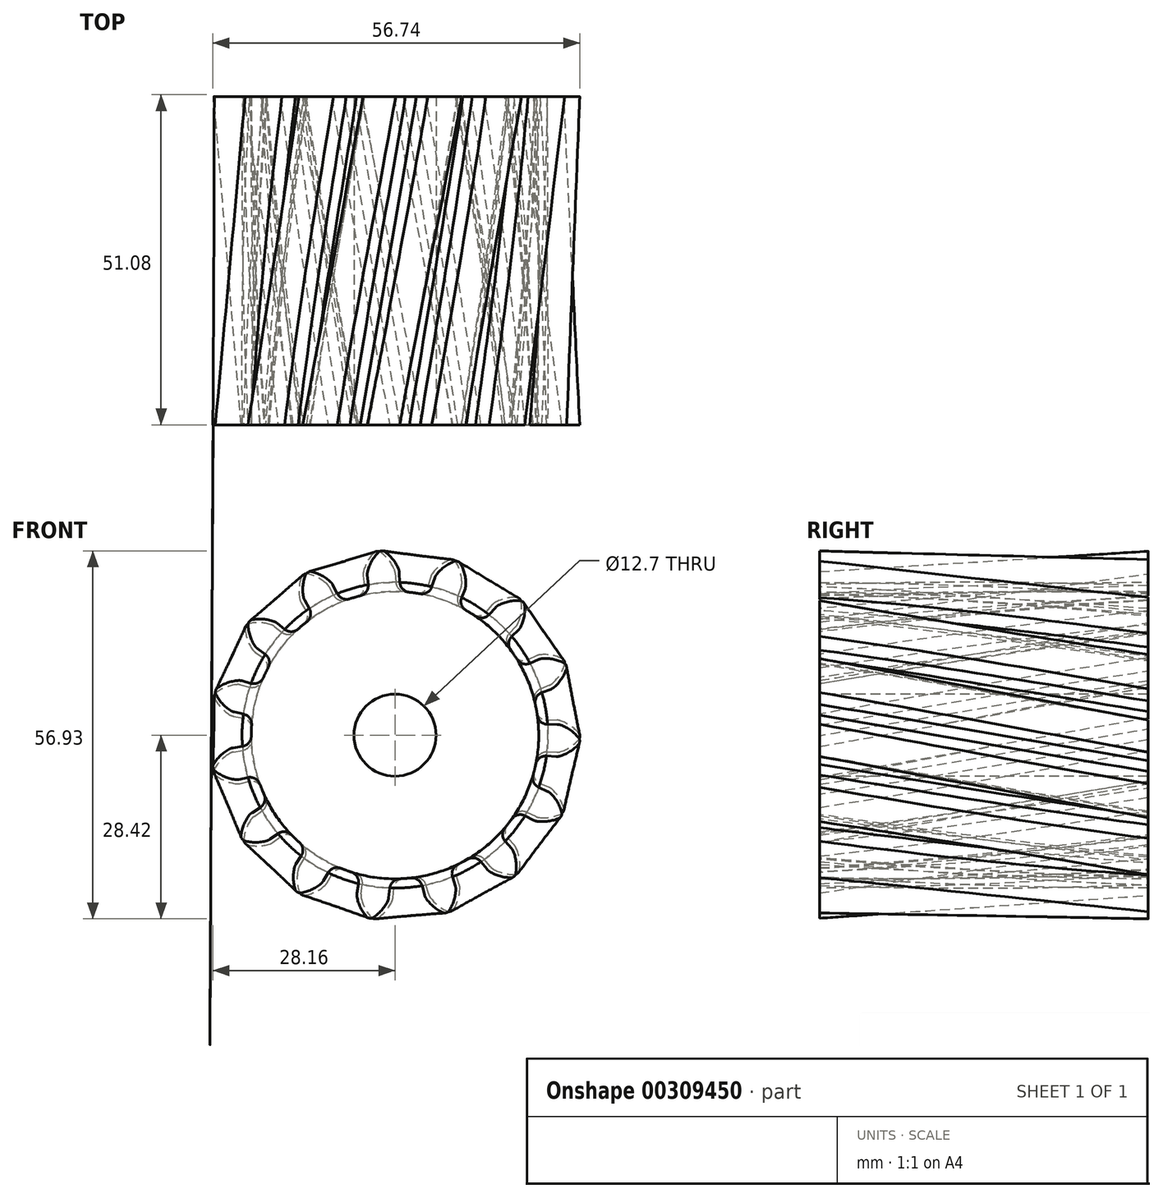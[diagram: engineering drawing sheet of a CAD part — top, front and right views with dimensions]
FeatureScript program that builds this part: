
annotation { "Feature Type Name" : "Feature", "Feature Type Description" : "" }
export const myFeature = defineFeature(function(context is Context, id is Id, definition is map)
    precondition{}
    {
        {
            var Q0;
            Q0=qCreatedBy(makeId("Front.planeOp"),FACE);
            var sketch = newSketch(context, id + "F0", { "sketchPlane" : qUnion([Q0])});
            skCircle(sketch, "E0", {"center": v(0, 0) * mm, "radius": 22.23 * mm});
            skArc(sketch, "E1.trimOffspring", {"start": v(-0.11, 25.67) * mm, "mid": v(-1.04, 27.17) * mm, "end": v(-2.34, 28.36) * mm});
            skLineSegment(sketch, "E2", {"start": v(0.02, 25.15) * mm, "end": v(0.23, 22.22) * mm});
            skLineSegment(sketch, "E3", {"start": v(-2.68, 28.45) * mm, "end": v(-2.8, 28.44) * mm});
            skLineSegment(sketch, "E4.MirrorCS", {"start": v(-2.93, 28.43) * mm, "end": v(-2.8, 28.44) * mm});
            skArc(sketch, "E5.MirrorCS", {"start": v(-4.9, 25.2) * mm, "mid": v(-4.28, 26.86) * mm, "end": v(-3.23, 28.28) * mm});
            skLineSegment(sketch, "E6.MirrorCS", {"start": v(-4.92, 24.66) * mm, "end": v(-4.56, 21.75) * mm});
            skPoint(sketch, "E7.visualSharp", {"position": v(0, 25.4) * mm});
            skArc(sketch, "E7.filletArc", {"start": v(0.02, 25.15) * mm, "mid": v(-0.02, 25.41) * mm, "end": v(-0.11, 25.67) * mm});
            skPoint(sketch, "E8.visualSharp", {"position": v(-4.96, 24.91) * mm});
            skArc(sketch, "E8.filletArc", {"start": v(-4.9, 25.2) * mm, "mid": v(-4.93, 24.93) * mm, "end": v(-4.92, 24.66) * mm});
            skPoint(sketch, "E9.visualSharp", {"position": v(-2.5, 28.47) * mm});
            skArc(sketch, "E9.filletArc", {"start": v(-2.34, 28.36) * mm, "mid": v(-2.5, 28.44) * mm, "end": v(-2.68, 28.45) * mm});
            skPoint(sketch, "E10.visualSharp", {"position": v(-3.1, 28.4) * mm});
            skArc(sketch, "E10.filletArc", {"start": v(-2.93, 28.43) * mm, "mid": v(-3.1, 28.38) * mm, "end": v(-3.23, 28.28) * mm});
            skSolve(sketch);
        }
        {
            var Q0;
            Q0=qCreatedBy(makeId("Front.planeOp"),FACE);
            cPlane(context, id + "F1", {"entities" : qUnion([Q0]), "cplaneType" : CPlaneType.OFFSET, "offset" : 50.8 * mm, "width" : 152.4 * mm, "height" : 152.4 * mm});
        }
        {
            var Q0;
            Q0=qCreatedBy(id+"F1.planeOp",FACE);
            var sketch = newSketch(context, id + "F2", { "sketchPlane" : qUnion([Q0])});
            skArc(sketch, "E11.0.0", {"start": v(-4.56, 21.75) * mm, "mid": v(2.18, -22.12) * mm, "end": v(0.23, 22.22) * mm});
            skArc(sketch, "E11.0.1", {"start": v(0.23, 22.22) * mm, "mid": v(-2.18, 22.12) * mm, "end": v(-4.56, 21.75) * mm});
            skArc(sketch, "E12.0.0", {"start": v(-3.23, 28.28) * mm, "mid": v(-4.28, 26.86) * mm, "end": v(-4.9, 25.2) * mm});
            skArc(sketch, "E12.0.1", {"start": v(-4.9, 25.2) * mm, "mid": v(-4.93, 24.93) * mm, "end": v(-4.92, 24.66) * mm});
            skLineSegment(sketch, "E12.0.2", {"start": v(-4.92, 24.66) * mm, "end": v(-4.56, 21.75) * mm});
            skArc(sketch, "E12.0.3", {"start": v(-4.56, 21.75) * mm, "mid": v(-2.18, 22.12) * mm, "end": v(0.23, 22.22) * mm});
            skLineSegment(sketch, "E12.0.4", {"start": v(0.23, 22.22) * mm, "end": v(0.02, 25.15) * mm});
            skArc(sketch, "E12.0.5", {"start": v(0.02, 25.15) * mm, "mid": v(-0.02, 25.41) * mm, "end": v(-0.11, 25.67) * mm});
            skArc(sketch, "E12.0.6", {"start": v(-0.11, 25.67) * mm, "mid": v(-1.04, 27.17) * mm, "end": v(-2.34, 28.36) * mm});
            skArc(sketch, "E12.0.7", {"start": v(-2.34, 28.36) * mm, "mid": v(-2.5, 28.44) * mm, "end": v(-2.68, 28.45) * mm});
            skLineSegment(sketch, "E12.0.8", {"start": v(-2.68, 28.45) * mm, "end": v(-2.8, 28.44) * mm});
            skLineSegment(sketch, "E12.0.9", {"start": v(-2.8, 28.44) * mm, "end": v(-2.93, 28.43) * mm});
            skArc(sketch, "E12.0.10", {"start": v(-2.93, 28.43) * mm, "mid": v(-3.1, 28.38) * mm, "end": v(-3.23, 28.28) * mm});
            skLineSegment(sketch, "E13.1.0", {"start": v(-8.3, 20.62) * mm, "end": v(-9.6, 23.24) * mm});
            skArc(sketch, "E13.1.1", {"start": v(-9.6, 23.24) * mm, "mid": v(-9.75, 23.47) * mm, "end": v(-9.93, 23.68) * mm});
            skArc(sketch, "E13.1.2", {"start": v(-9.93, 23.68) * mm, "mid": v(-11.36, 24.7) * mm, "end": v(-13.02, 25.3) * mm});
            skArc(sketch, "E13.1.3", {"start": v(-14.17, 21.4) * mm, "mid": v(-14.1, 21.15) * mm, "end": v(-13.99, 20.9) * mm});
            skLineSegment(sketch, "E13.1.4", {"start": v(-13.99, 20.9) * mm, "end": v(-12.54, 18.35) * mm});
            skArc(sketch, "E13.1.5", {"start": v(-13.8, 24.89) * mm, "mid": v(-14.23, 23.17) * mm, "end": v(-14.17, 21.4) * mm});
            skArc(sketch, "E13.1.6", {"start": v(-13.02, 25.3) * mm, "mid": v(-13.2, 25.31) * mm, "end": v(-13.36, 25.26) * mm});
            skLineSegment(sketch, "E13.1.7", {"start": v(-13.36, 25.26) * mm, "end": v(-13.47, 25.2) * mm});
            skLineSegment(sketch, "E13.1.8", {"start": v(-13.47, 25.2) * mm, "end": v(-13.58, 25.14) * mm});
            skArc(sketch, "E13.1.9", {"start": v(-13.58, 25.14) * mm, "mid": v(-13.72, 25.03) * mm, "end": v(-13.8, 24.89) * mm});
            skLineSegment(sketch, "E13.2.0", {"start": v(-15.55, 15.88) * mm, "end": v(-17.77, 17.8) * mm});
            skArc(sketch, "E13.2.1", {"start": v(-17.77, 17.8) * mm, "mid": v(-17.99, 17.95) * mm, "end": v(-18.23, 18.07) * mm});
            skArc(sketch, "E13.2.2", {"start": v(-18.23, 18.07) * mm, "mid": v(-19.95, 18.48) * mm, "end": v(-21.71, 18.4) * mm});
            skArc(sketch, "E13.2.3", {"start": v(-21.28, 14.36) * mm, "mid": v(-21.12, 14.14) * mm, "end": v(-20.92, 13.95) * mm});
            skLineSegment(sketch, "E13.2.4", {"start": v(-20.92, 13.95) * mm, "end": v(-18.6, 12.15) * mm});
            skArc(sketch, "E13.2.5", {"start": v(-22.28, 17.7) * mm, "mid": v(-22.02, 15.96) * mm, "end": v(-21.28, 14.36) * mm});
            skArc(sketch, "E13.2.6", {"start": v(-21.71, 18.4) * mm, "mid": v(-21.88, 18.34) * mm, "end": v(-22, 18.23) * mm});
            skLineSegment(sketch, "E13.2.7", {"start": v(-22, 18.23) * mm, "end": v(-22.1, 18.13) * mm});
            skLineSegment(sketch, "E13.2.8", {"start": v(-22.1, 18.13) * mm, "end": v(-22.17, 18.03) * mm});
            skArc(sketch, "E13.2.9", {"start": v(-22.17, 18.03) * mm, "mid": v(-22.25, 17.88) * mm, "end": v(-22.28, 17.7) * mm});
            skLineSegment(sketch, "E13.3.0", {"start": v(-20.44, 8.72) * mm, "end": v(-23.22, 9.64) * mm});
            skArc(sketch, "E13.3.1", {"start": v(-23.22, 9.64) * mm, "mid": v(-23.49, 9.7) * mm, "end": v(-23.76, 9.72) * mm});
            skArc(sketch, "E13.3.2", {"start": v(-23.76, 9.72) * mm, "mid": v(-25.5, 9.44) * mm, "end": v(-27.1, 8.69) * mm});
            skArc(sketch, "E13.3.3", {"start": v(-25.16, 5.12) * mm, "mid": v(-24.92, 4.98) * mm, "end": v(-24.67, 4.89) * mm});
            skLineSegment(sketch, "E13.3.4", {"start": v(-24.67, 4.89) * mm, "end": v(-21.84, 4.1) * mm});
            skArc(sketch, "E13.3.5", {"start": v(-27.36, 7.83) * mm, "mid": v(-26.45, 6.32) * mm, "end": v(-25.16, 5.12) * mm});
            skArc(sketch, "E13.3.6", {"start": v(-27.1, 8.69) * mm, "mid": v(-27.23, 8.57) * mm, "end": v(-27.3, 8.42) * mm});
            skLineSegment(sketch, "E13.3.7", {"start": v(-27.3, 8.42) * mm, "end": v(-27.35, 8.3) * mm});
            skLineSegment(sketch, "E13.3.8", {"start": v(-27.35, 8.3) * mm, "end": v(-27.38, 8.17) * mm});
            skArc(sketch, "E13.3.9", {"start": v(-27.38, 8.17) * mm, "mid": v(-27.4, 8) * mm, "end": v(-27.36, 7.83) * mm});
            skLineSegment(sketch, "E13.4.0", {"start": v(-22.22, 0.23) * mm, "end": v(-25.15, 0.02) * mm});
            skArc(sketch, "E13.4.1", {"start": v(-25.15, 0.02) * mm, "mid": v(-25.41, -0.02) * mm, "end": v(-25.67, -0.11) * mm});
            skArc(sketch, "E13.4.2", {"start": v(-25.67, -0.11) * mm, "mid": v(-27.17, -1.04) * mm, "end": v(-28.36, -2.34) * mm});
            skArc(sketch, "E13.4.3", {"start": v(-25.2, -4.9) * mm, "mid": v(-24.93, -4.93) * mm, "end": v(-24.66, -4.92) * mm});
            skLineSegment(sketch, "E13.4.4", {"start": v(-24.66, -4.92) * mm, "end": v(-21.75, -4.56) * mm});
            skArc(sketch, "E13.4.5", {"start": v(-28.28, -3.23) * mm, "mid": v(-26.86, -4.28) * mm, "end": v(-25.2, -4.9) * mm});
            skArc(sketch, "E13.4.6", {"start": v(-28.36, -2.34) * mm, "mid": v(-28.44, -2.5) * mm, "end": v(-28.45, -2.68) * mm});
            skLineSegment(sketch, "E13.4.7", {"start": v(-28.45, -2.68) * mm, "end": v(-28.44, -2.8) * mm});
            skLineSegment(sketch, "E13.4.8", {"start": v(-28.44, -2.8) * mm, "end": v(-28.43, -2.93) * mm});
            skArc(sketch, "E13.4.9", {"start": v(-28.43, -2.93) * mm, "mid": v(-28.38, -3.1) * mm, "end": v(-28.28, -3.23) * mm});
            skLineSegment(sketch, "E13.5.0", {"start": v(-20.62, -8.3) * mm, "end": v(-23.24, -9.6) * mm});
            skArc(sketch, "E13.5.1", {"start": v(-23.24, -9.6) * mm, "mid": v(-23.47, -9.75) * mm, "end": v(-23.68, -9.93) * mm});
            skArc(sketch, "E13.5.2", {"start": v(-23.68, -9.93) * mm, "mid": v(-24.7, -11.36) * mm, "end": v(-25.3, -13.02) * mm});
            skArc(sketch, "E13.5.3", {"start": v(-21.4, -14.17) * mm, "mid": v(-21.15, -14.1) * mm, "end": v(-20.9, -13.99) * mm});
            skLineSegment(sketch, "E13.5.4", {"start": v(-20.9, -13.99) * mm, "end": v(-18.35, -12.54) * mm});
            skArc(sketch, "E13.5.5", {"start": v(-24.89, -13.8) * mm, "mid": v(-23.17, -14.23) * mm, "end": v(-21.4, -14.17) * mm});
            skArc(sketch, "E13.5.6", {"start": v(-25.3, -13.02) * mm, "mid": v(-25.31, -13.2) * mm, "end": v(-25.26, -13.36) * mm});
            skLineSegment(sketch, "E13.5.7", {"start": v(-25.26, -13.36) * mm, "end": v(-25.2, -13.47) * mm});
            skLineSegment(sketch, "E13.5.8", {"start": v(-25.2, -13.47) * mm, "end": v(-25.14, -13.58) * mm});
            skArc(sketch, "E13.5.9", {"start": v(-25.14, -13.58) * mm, "mid": v(-25.03, -13.72) * mm, "end": v(-24.89, -13.8) * mm});
            skLineSegment(sketch, "E13.6.0", {"start": v(-15.88, -15.55) * mm, "end": v(-17.8, -17.77) * mm});
            skArc(sketch, "E13.6.1", {"start": v(-17.8, -17.77) * mm, "mid": v(-17.95, -17.99) * mm, "end": v(-18.07, -18.23) * mm});
            skArc(sketch, "E13.6.2", {"start": v(-18.07, -18.23) * mm, "mid": v(-18.48, -19.95) * mm, "end": v(-18.4, -21.71) * mm});
            skArc(sketch, "E13.6.3", {"start": v(-14.36, -21.28) * mm, "mid": v(-14.14, -21.12) * mm, "end": v(-13.95, -20.92) * mm});
            skLineSegment(sketch, "E13.6.4", {"start": v(-13.95, -20.92) * mm, "end": v(-12.15, -18.6) * mm});
            skArc(sketch, "E13.6.5", {"start": v(-17.7, -22.28) * mm, "mid": v(-15.96, -22.02) * mm, "end": v(-14.36, -21.28) * mm});
            skArc(sketch, "E13.6.6", {"start": v(-18.4, -21.71) * mm, "mid": v(-18.34, -21.88) * mm, "end": v(-18.23, -22) * mm});
            skLineSegment(sketch, "E13.6.7", {"start": v(-18.23, -22) * mm, "end": v(-18.13, -22.1) * mm});
            skLineSegment(sketch, "E13.6.8", {"start": v(-18.13, -22.1) * mm, "end": v(-18.03, -22.17) * mm});
            skArc(sketch, "E13.6.9", {"start": v(-18.03, -22.17) * mm, "mid": v(-17.88, -22.25) * mm, "end": v(-17.7, -22.28) * mm});
            skLineSegment(sketch, "E13.7.0", {"start": v(-8.72, -20.44) * mm, "end": v(-9.64, -23.22) * mm});
            skArc(sketch, "E13.7.1", {"start": v(-9.64, -23.22) * mm, "mid": v(-9.7, -23.49) * mm, "end": v(-9.72, -23.76) * mm});
            skArc(sketch, "E13.7.2", {"start": v(-9.72, -23.76) * mm, "mid": v(-9.44, -25.5) * mm, "end": v(-8.69, -27.1) * mm});
            skArc(sketch, "E13.7.3", {"start": v(-5.12, -25.16) * mm, "mid": v(-4.98, -24.92) * mm, "end": v(-4.89, -24.67) * mm});
            skLineSegment(sketch, "E13.7.4", {"start": v(-4.89, -24.67) * mm, "end": v(-4.1, -21.84) * mm});
            skArc(sketch, "E13.7.5", {"start": v(-7.83, -27.36) * mm, "mid": v(-6.32, -26.45) * mm, "end": v(-5.12, -25.16) * mm});
            skArc(sketch, "E13.7.6", {"start": v(-8.69, -27.1) * mm, "mid": v(-8.57, -27.23) * mm, "end": v(-8.42, -27.3) * mm});
            skLineSegment(sketch, "E13.7.7", {"start": v(-8.42, -27.3) * mm, "end": v(-8.3, -27.35) * mm});
            skLineSegment(sketch, "E13.7.8", {"start": v(-8.3, -27.35) * mm, "end": v(-8.17, -27.38) * mm});
            skArc(sketch, "E13.7.9", {"start": v(-8.17, -27.38) * mm, "mid": v(-8, -27.4) * mm, "end": v(-7.83, -27.36) * mm});
            skLineSegment(sketch, "E13.8.0", {"start": v(-0.23, -22.22) * mm, "end": v(-0.02, -25.15) * mm});
            skArc(sketch, "E13.8.1", {"start": v(-0.02, -25.15) * mm, "mid": v(0.02, -25.41) * mm, "end": v(0.11, -25.67) * mm});
            skArc(sketch, "E13.8.2", {"start": v(0.11, -25.67) * mm, "mid": v(1.04, -27.17) * mm, "end": v(2.34, -28.36) * mm});
            skArc(sketch, "E13.8.3", {"start": v(4.9, -25.2) * mm, "mid": v(4.93, -24.93) * mm, "end": v(4.92, -24.66) * mm});
            skLineSegment(sketch, "E13.8.4", {"start": v(4.92, -24.66) * mm, "end": v(4.56, -21.75) * mm});
            skArc(sketch, "E13.8.5", {"start": v(3.23, -28.28) * mm, "mid": v(4.28, -26.86) * mm, "end": v(4.9, -25.2) * mm});
            skArc(sketch, "E13.8.6", {"start": v(2.34, -28.36) * mm, "mid": v(2.5, -28.44) * mm, "end": v(2.68, -28.45) * mm});
            skLineSegment(sketch, "E13.8.7", {"start": v(2.68, -28.45) * mm, "end": v(2.8, -28.44) * mm});
            skLineSegment(sketch, "E13.8.8", {"start": v(2.8, -28.44) * mm, "end": v(2.93, -28.43) * mm});
            skArc(sketch, "E13.8.9", {"start": v(2.93, -28.43) * mm, "mid": v(3.1, -28.38) * mm, "end": v(3.23, -28.28) * mm});
            skLineSegment(sketch, "E13.9.0", {"start": v(8.3, -20.62) * mm, "end": v(9.6, -23.24) * mm});
            skArc(sketch, "E13.9.1", {"start": v(9.6, -23.24) * mm, "mid": v(9.75, -23.47) * mm, "end": v(9.93, -23.68) * mm});
            skArc(sketch, "E13.9.2", {"start": v(9.93, -23.68) * mm, "mid": v(11.36, -24.7) * mm, "end": v(13.02, -25.3) * mm});
            skArc(sketch, "E13.9.3", {"start": v(14.17, -21.4) * mm, "mid": v(14.1, -21.15) * mm, "end": v(13.99, -20.9) * mm});
            skLineSegment(sketch, "E13.9.4", {"start": v(13.99, -20.9) * mm, "end": v(12.54, -18.35) * mm});
            skArc(sketch, "E13.9.5", {"start": v(13.8, -24.89) * mm, "mid": v(14.23, -23.17) * mm, "end": v(14.17, -21.4) * mm});
            skArc(sketch, "E13.9.6", {"start": v(13.02, -25.3) * mm, "mid": v(13.2, -25.31) * mm, "end": v(13.36, -25.26) * mm});
            skLineSegment(sketch, "E13.9.7", {"start": v(13.36, -25.26) * mm, "end": v(13.47, -25.2) * mm});
            skLineSegment(sketch, "E13.9.8", {"start": v(13.47, -25.2) * mm, "end": v(13.58, -25.14) * mm});
            skArc(sketch, "E13.9.9", {"start": v(13.58, -25.14) * mm, "mid": v(13.72, -25.03) * mm, "end": v(13.8, -24.89) * mm});
            skLineSegment(sketch, "E13.10.0", {"start": v(15.55, -15.88) * mm, "end": v(17.77, -17.8) * mm});
            skArc(sketch, "E13.10.1", {"start": v(17.77, -17.8) * mm, "mid": v(17.99, -17.95) * mm, "end": v(18.23, -18.07) * mm});
            skArc(sketch, "E13.10.2", {"start": v(18.23, -18.07) * mm, "mid": v(19.95, -18.48) * mm, "end": v(21.71, -18.4) * mm});
            skArc(sketch, "E13.10.3", {"start": v(21.28, -14.36) * mm, "mid": v(21.12, -14.14) * mm, "end": v(20.92, -13.95) * mm});
            skLineSegment(sketch, "E13.10.4", {"start": v(20.92, -13.95) * mm, "end": v(18.6, -12.15) * mm});
            skArc(sketch, "E13.10.5", {"start": v(22.28, -17.7) * mm, "mid": v(22.02, -15.96) * mm, "end": v(21.28, -14.36) * mm});
            skArc(sketch, "E13.10.6", {"start": v(21.71, -18.4) * mm, "mid": v(21.88, -18.34) * mm, "end": v(22, -18.23) * mm});
            skLineSegment(sketch, "E13.10.7", {"start": v(22, -18.23) * mm, "end": v(22.1, -18.13) * mm});
            skLineSegment(sketch, "E13.10.8", {"start": v(22.1, -18.13) * mm, "end": v(22.17, -18.03) * mm});
            skArc(sketch, "E13.10.9", {"start": v(22.17, -18.03) * mm, "mid": v(22.25, -17.88) * mm, "end": v(22.28, -17.7) * mm});
            skLineSegment(sketch, "E13.11.0", {"start": v(20.44, -8.72) * mm, "end": v(23.22, -9.64) * mm});
            skArc(sketch, "E13.11.1", {"start": v(23.22, -9.64) * mm, "mid": v(23.49, -9.7) * mm, "end": v(23.76, -9.72) * mm});
            skArc(sketch, "E13.11.2", {"start": v(23.76, -9.72) * mm, "mid": v(25.5, -9.44) * mm, "end": v(27.1, -8.69) * mm});
            skArc(sketch, "E13.11.3", {"start": v(25.16, -5.12) * mm, "mid": v(24.92, -4.98) * mm, "end": v(24.67, -4.89) * mm});
            skLineSegment(sketch, "E13.11.4", {"start": v(24.67, -4.89) * mm, "end": v(21.84, -4.1) * mm});
            skArc(sketch, "E13.11.5", {"start": v(27.36, -7.83) * mm, "mid": v(26.45, -6.32) * mm, "end": v(25.16, -5.12) * mm});
            skArc(sketch, "E13.11.6", {"start": v(27.1, -8.69) * mm, "mid": v(27.23, -8.57) * mm, "end": v(27.3, -8.42) * mm});
            skLineSegment(sketch, "E13.11.7", {"start": v(27.3, -8.42) * mm, "end": v(27.35, -8.3) * mm});
            skLineSegment(sketch, "E13.11.8", {"start": v(27.35, -8.3) * mm, "end": v(27.38, -8.17) * mm});
            skArc(sketch, "E13.11.9", {"start": v(27.38, -8.17) * mm, "mid": v(27.4, -8) * mm, "end": v(27.36, -7.83) * mm});
            skLineSegment(sketch, "E13.12.0", {"start": v(22.22, -0.23) * mm, "end": v(25.15, -0.02) * mm});
            skArc(sketch, "E13.12.1", {"start": v(25.15, -0.02) * mm, "mid": v(25.41, 0.02) * mm, "end": v(25.67, 0.11) * mm});
            skArc(sketch, "E13.12.2", {"start": v(25.67, 0.11) * mm, "mid": v(27.17, 1.04) * mm, "end": v(28.36, 2.34) * mm});
            skArc(sketch, "E13.12.3", {"start": v(25.2, 4.9) * mm, "mid": v(24.93, 4.93) * mm, "end": v(24.66, 4.92) * mm});
            skLineSegment(sketch, "E13.12.4", {"start": v(24.66, 4.92) * mm, "end": v(21.75, 4.56) * mm});
            skArc(sketch, "E13.12.5", {"start": v(28.28, 3.23) * mm, "mid": v(26.86, 4.28) * mm, "end": v(25.2, 4.9) * mm});
            skArc(sketch, "E13.12.6", {"start": v(28.36, 2.34) * mm, "mid": v(28.44, 2.5) * mm, "end": v(28.45, 2.68) * mm});
            skLineSegment(sketch, "E13.12.7", {"start": v(28.45, 2.68) * mm, "end": v(28.44, 2.8) * mm});
            skLineSegment(sketch, "E13.12.8", {"start": v(28.44, 2.8) * mm, "end": v(28.43, 2.93) * mm});
            skArc(sketch, "E13.12.9", {"start": v(28.43, 2.93) * mm, "mid": v(28.38, 3.1) * mm, "end": v(28.28, 3.23) * mm});
            skLineSegment(sketch, "E13.13.0", {"start": v(20.62, 8.3) * mm, "end": v(23.24, 9.6) * mm});
            skArc(sketch, "E13.13.1", {"start": v(23.24, 9.6) * mm, "mid": v(23.47, 9.75) * mm, "end": v(23.68, 9.93) * mm});
            skArc(sketch, "E13.13.2", {"start": v(23.68, 9.93) * mm, "mid": v(24.7, 11.36) * mm, "end": v(25.3, 13.02) * mm});
            skArc(sketch, "E13.13.3", {"start": v(21.4, 14.17) * mm, "mid": v(21.15, 14.1) * mm, "end": v(20.9, 13.99) * mm});
            skLineSegment(sketch, "E13.13.4", {"start": v(20.9, 13.99) * mm, "end": v(18.35, 12.54) * mm});
            skArc(sketch, "E13.13.5", {"start": v(24.89, 13.8) * mm, "mid": v(23.17, 14.23) * mm, "end": v(21.4, 14.17) * mm});
            skArc(sketch, "E13.13.6", {"start": v(25.3, 13.02) * mm, "mid": v(25.31, 13.2) * mm, "end": v(25.26, 13.36) * mm});
            skLineSegment(sketch, "E13.13.7", {"start": v(25.26, 13.36) * mm, "end": v(25.2, 13.47) * mm});
            skLineSegment(sketch, "E13.13.8", {"start": v(25.2, 13.47) * mm, "end": v(25.14, 13.58) * mm});
            skArc(sketch, "E13.13.9", {"start": v(25.14, 13.58) * mm, "mid": v(25.03, 13.72) * mm, "end": v(24.89, 13.8) * mm});
            skLineSegment(sketch, "E13.14.0", {"start": v(15.88, 15.55) * mm, "end": v(17.8, 17.77) * mm});
            skArc(sketch, "E13.14.1", {"start": v(17.8, 17.77) * mm, "mid": v(17.95, 17.99) * mm, "end": v(18.07, 18.23) * mm});
            skArc(sketch, "E13.14.2", {"start": v(18.07, 18.23) * mm, "mid": v(18.48, 19.95) * mm, "end": v(18.4, 21.71) * mm});
            skArc(sketch, "E13.14.3", {"start": v(14.36, 21.28) * mm, "mid": v(14.14, 21.12) * mm, "end": v(13.95, 20.92) * mm});
            skLineSegment(sketch, "E13.14.4", {"start": v(13.95, 20.92) * mm, "end": v(12.15, 18.6) * mm});
            skArc(sketch, "E13.14.5", {"start": v(17.7, 22.28) * mm, "mid": v(15.96, 22.02) * mm, "end": v(14.36, 21.28) * mm});
            skArc(sketch, "E13.14.6", {"start": v(18.4, 21.71) * mm, "mid": v(18.34, 21.88) * mm, "end": v(18.23, 22) * mm});
            skLineSegment(sketch, "E13.14.7", {"start": v(18.23, 22) * mm, "end": v(18.13, 22.1) * mm});
            skLineSegment(sketch, "E13.14.8", {"start": v(18.13, 22.1) * mm, "end": v(18.03, 22.17) * mm});
            skArc(sketch, "E13.14.9", {"start": v(18.03, 22.17) * mm, "mid": v(17.88, 22.25) * mm, "end": v(17.7, 22.28) * mm});
            skLineSegment(sketch, "E13.15.0", {"start": v(8.72, 20.44) * mm, "end": v(9.64, 23.22) * mm});
            skArc(sketch, "E13.15.1", {"start": v(9.64, 23.22) * mm, "mid": v(9.7, 23.49) * mm, "end": v(9.72, 23.76) * mm});
            skArc(sketch, "E13.15.2", {"start": v(9.72, 23.76) * mm, "mid": v(9.44, 25.5) * mm, "end": v(8.69, 27.1) * mm});
            skArc(sketch, "E13.15.3", {"start": v(5.12, 25.16) * mm, "mid": v(4.98, 24.92) * mm, "end": v(4.89, 24.67) * mm});
            skLineSegment(sketch, "E13.15.4", {"start": v(4.89, 24.67) * mm, "end": v(4.1, 21.84) * mm});
            skArc(sketch, "E13.15.5", {"start": v(7.83, 27.36) * mm, "mid": v(6.32, 26.45) * mm, "end": v(5.12, 25.16) * mm});
            skArc(sketch, "E13.15.6", {"start": v(8.69, 27.1) * mm, "mid": v(8.57, 27.23) * mm, "end": v(8.42, 27.3) * mm});
            skLineSegment(sketch, "E13.15.7", {"start": v(8.42, 27.3) * mm, "end": v(8.3, 27.35) * mm});
            skLineSegment(sketch, "E13.15.8", {"start": v(8.3, 27.35) * mm, "end": v(8.17, 27.38) * mm});
            skArc(sketch, "E13.15.9", {"start": v(8.17, 27.38) * mm, "mid": v(8, 27.4) * mm, "end": v(7.83, 27.36) * mm});
            skSolve(sketch);
        }
        {
            var Q0;
            {var subQ0=sQuery(id+"F2.wireOp",EDGE,"E13.1.0");Q0=makeQuery(id+"F2.imprint","IMPRINT",FACE,{"disambiguationData":[TD([[makeQuery(id+"F2.imprint","IMPRINT",EDGE,{"derivedFrom":subQ0}),1.0]])]});}
            var Q1;
            Q1=makeQuery(id+"F0.imprint","IMPRINT",FACE,{"disambiguationData":[TD([[makeQuery(id+"F0.imprint","IMPRINT",EDGE,{"derivedFrom":sQuery(id+"F0.wireOp",EDGE,"E1.trimOffspring")}),1.0]])]});
            loft(context, id + "F3", {"sheetProfilesArray" : [{ "sheetProfileEntities" : qUnion([Q0]) }, { "sheetProfileEntities" : qUnion([Q1]) }]});
        }
        {
            var Q0;
            Q0=qCreatedBy(makeId("Front.planeOp"),FACE);
            var sketch = newSketch(context, id + "F4", { "sketchPlane" : qUnion([Q0])});
            skCircle(sketch, "E14", {"center": v(0, 0) * mm, "radius": 22.23 * mm});
            skSolve(sketch);
        }
        {
            var Q0;
            Q0=makeQuery(id+"F4.imprint","IMPRINT",FACE,{"disambiguationData":[TD([[makeQuery(id+"F4.imprint","IMPRINT",EDGE,{"derivedFrom":sQuery(id+"F4.wireOp",EDGE,"E14")}),1.0]])]});
            var Q1;
            {var subQ0=sQuery(id+"F2.wireOp",EDGE,"E13.1.0");Q1=makeQuery(id+"F3.opLoft","CAP_FACE",FACE,{"disambiguationData":[OSD([makeQuery(id+"F2.imprint","IMPRINT",FACE,{"disambiguationData":[TD([[makeQuery(id+"F2.imprint","IMPRINT",EDGE,{"derivedFrom":subQ0}),1.0]])]})])],"isStart":true});}
            extrude(context, id + "F5", {"entities" : qUnion([Q0]), "operationType" : NewBodyOperationType.ADD, "endBound" : BoundingType.UP_TO_SURFACE, "endBoundEntityFace" : qUnion([Q1]), "depth" : 25.4 * mm});
        }
        {
            var Q0;
            {var subQ0=sQuery(id+"F2.wireOp",EDGE,"E13.1.0");Q0=makeQuery(id+"F3.opLoft","SWEPT_BODY",BODY,{"disambiguationData":[OSD([makeQuery(id+"F0.imprint","IMPRINT",FACE,{"disambiguationData":[TD([[makeQuery(id+"F0.imprint","IMPRINT",EDGE,{"derivedFrom":sQuery(id+"F0.wireOp",EDGE,"E1.trimOffspring")}),1.0]])]}),makeQuery(id+"F2.imprint","IMPRINT",FACE,{"disambiguationData":[TD([[makeQuery(id+"F2.imprint","IMPRINT",EDGE,{"derivedFrom":subQ0}),1.0]])]})])]});}
            var Q1;
            Q1=makeQuery(id+"F5.opExtrude","SWEPT_FACE",FACE,{"disambiguationData":[OSD([sQuery(id+"F4.wireOp",EDGE,"E14")])]});
            circularPattern(context, id + "F6", {"entities" : qUnion([Q0]), "axis" : qUnion([Q1]), "angle" : 360 * degree, "instanceCount" : 15, "equalSpace" : true});
        }
        {
            var Q0;
            Q0=makeQuery(id+"F6.opPattern","COPY",EDGE,{"derivedFrom":makeQuery(id+"F5.boolean.opBoolean","INTERSECT",EDGE,{"derivedFrom":[makeQuery(id+"F3.opLoft","SWEPT_FACE",FACE,{"disambiguationData":[OSD([sQuery(id+"F0.wireOp",EDGE,"E3"),sQuery(id+"F0.wireOp",EDGE,"E4.MirrorCS"),sQuery(id+"F0.wireOp",EDGE,"E9.filletArc"),sQuery(id+"F2.wireOp",EDGE,"E13.1.6"),sQuery(id+"F2.wireOp",EDGE,"E13.1.7"),sQuery(id+"F2.wireOp",EDGE,"E13.1.8")])]}),makeQuery(id+"F5.opExtrude","SWEPT_FACE",FACE,{"disambiguationData":[OSD([sQuery(id+"F4.wireOp",EDGE,"E14")])]})]}),"instanceName":"1"});
            var Q1;
            Q1=makeQuery(id+"F6.opPattern","COPY",EDGE,{"derivedFrom":makeQuery(id+"F5.boolean.opBoolean","INTERSECT",EDGE,{"derivedFrom":[makeQuery(id+"F3.opLoft","SWEPT_FACE",FACE,{"disambiguationData":[OSD([sQuery(id+"F0.wireOp",EDGE,"E0"),sQuery(id+"F0.wireOp",EDGE,"E6.MirrorCS"),sQuery(id+"F0.wireOp",EDGE,"E8.filletArc"),sQuery(id+"F2.wireOp",EDGE,"E11.0.0"),sQuery(id+"F2.wireOp",EDGE,"E13.1.3"),sQuery(id+"F2.wireOp",EDGE,"E13.1.4")])]}),makeQuery(id+"F5.opExtrude","SWEPT_FACE",FACE,{"disambiguationData":[OSD([sQuery(id+"F4.wireOp",EDGE,"E14")])]})]}),"instanceName":"9"});
            var Q2;
            Q2=makeQuery(id+"F6.opPattern","COPY",EDGE,{"derivedFrom":makeQuery(id+"F5.boolean.opBoolean","INTERSECT",EDGE,{"derivedFrom":[makeQuery(id+"F3.opLoft","SWEPT_FACE",FACE,{"disambiguationData":[OSD([sQuery(id+"F0.wireOp",EDGE,"E0"),sQuery(id+"F0.wireOp",EDGE,"E6.MirrorCS"),sQuery(id+"F0.wireOp",EDGE,"E8.filletArc"),sQuery(id+"F2.wireOp",EDGE,"E11.0.0"),sQuery(id+"F2.wireOp",EDGE,"E13.1.3"),sQuery(id+"F2.wireOp",EDGE,"E13.1.4")])]}),makeQuery(id+"F5.opExtrude","SWEPT_FACE",FACE,{"disambiguationData":[OSD([sQuery(id+"F4.wireOp",EDGE,"E14")])]})]}),"instanceName":"10"});
            var Q3;
            Q3=makeQuery(id+"F6.opPattern","COPY",EDGE,{"derivedFrom":makeQuery(id+"F5.boolean.opBoolean","INTERSECT",EDGE,{"derivedFrom":[makeQuery(id+"F3.opLoft","SWEPT_FACE",FACE,{"disambiguationData":[OSD([sQuery(id+"F0.wireOp",EDGE,"E0"),sQuery(id+"F0.wireOp",EDGE,"E6.MirrorCS"),sQuery(id+"F0.wireOp",EDGE,"E8.filletArc"),sQuery(id+"F2.wireOp",EDGE,"E11.0.0"),sQuery(id+"F2.wireOp",EDGE,"E13.1.3"),sQuery(id+"F2.wireOp",EDGE,"E13.1.4")])]}),makeQuery(id+"F5.opExtrude","SWEPT_FACE",FACE,{"disambiguationData":[OSD([sQuery(id+"F4.wireOp",EDGE,"E14")])]})]}),"instanceName":"8"});
            var Q4;
            Q4=makeQuery(id+"F6.opPattern","COPY",EDGE,{"derivedFrom":makeQuery(id+"F5.boolean.opBoolean","INTERSECT",EDGE,{"derivedFrom":[makeQuery(id+"F3.opLoft","SWEPT_FACE",FACE,{"disambiguationData":[OSD([sQuery(id+"F0.wireOp",EDGE,"E3"),sQuery(id+"F0.wireOp",EDGE,"E4.MirrorCS"),sQuery(id+"F0.wireOp",EDGE,"E9.filletArc"),sQuery(id+"F2.wireOp",EDGE,"E13.1.6"),sQuery(id+"F2.wireOp",EDGE,"E13.1.7"),sQuery(id+"F2.wireOp",EDGE,"E13.1.8")])]}),makeQuery(id+"F5.opExtrude","SWEPT_FACE",FACE,{"disambiguationData":[OSD([sQuery(id+"F4.wireOp",EDGE,"E14")])]})]}),"instanceName":"8"});
            var Q5;
            Q5=makeQuery(id+"F6.opPattern","COPY",EDGE,{"derivedFrom":makeQuery(id+"F5.boolean.opBoolean","INTERSECT",EDGE,{"derivedFrom":[makeQuery(id+"F3.opLoft","SWEPT_FACE",FACE,{"disambiguationData":[OSD([sQuery(id+"F0.wireOp",EDGE,"E3"),sQuery(id+"F0.wireOp",EDGE,"E4.MirrorCS"),sQuery(id+"F0.wireOp",EDGE,"E9.filletArc"),sQuery(id+"F2.wireOp",EDGE,"E13.1.6"),sQuery(id+"F2.wireOp",EDGE,"E13.1.7"),sQuery(id+"F2.wireOp",EDGE,"E13.1.8")])]}),makeQuery(id+"F5.opExtrude","SWEPT_FACE",FACE,{"disambiguationData":[OSD([sQuery(id+"F4.wireOp",EDGE,"E14")])]})]}),"instanceName":"9"});
            var Q6;
            Q6=makeQuery(id+"F6.opPattern","COPY",EDGE,{"derivedFrom":makeQuery(id+"F5.boolean.opBoolean","INTERSECT",EDGE,{"derivedFrom":[makeQuery(id+"F3.opLoft","SWEPT_FACE",FACE,{"disambiguationData":[OSD([sQuery(id+"F0.wireOp",EDGE,"E3"),sQuery(id+"F0.wireOp",EDGE,"E4.MirrorCS"),sQuery(id+"F0.wireOp",EDGE,"E9.filletArc"),sQuery(id+"F2.wireOp",EDGE,"E13.1.6"),sQuery(id+"F2.wireOp",EDGE,"E13.1.7"),sQuery(id+"F2.wireOp",EDGE,"E13.1.8")])]}),makeQuery(id+"F5.opExtrude","SWEPT_FACE",FACE,{"disambiguationData":[OSD([sQuery(id+"F4.wireOp",EDGE,"E14")])]})]}),"instanceName":"7"});
            var Q7;
            Q7=makeQuery(id+"F6.opPattern","COPY",EDGE,{"derivedFrom":makeQuery(id+"F5.boolean.opBoolean","INTERSECT",EDGE,{"derivedFrom":[makeQuery(id+"F3.opLoft","SWEPT_FACE",FACE,{"disambiguationData":[OSD([sQuery(id+"F0.wireOp",EDGE,"E0"),sQuery(id+"F0.wireOp",EDGE,"E6.MirrorCS"),sQuery(id+"F0.wireOp",EDGE,"E8.filletArc"),sQuery(id+"F2.wireOp",EDGE,"E11.0.0"),sQuery(id+"F2.wireOp",EDGE,"E13.1.3"),sQuery(id+"F2.wireOp",EDGE,"E13.1.4")])]}),makeQuery(id+"F5.opExtrude","SWEPT_FACE",FACE,{"disambiguationData":[OSD([sQuery(id+"F4.wireOp",EDGE,"E14")])]})]}),"instanceName":"7"});
            var Q8;
            Q8=makeQuery(id+"F6.opPattern","COPY",EDGE,{"derivedFrom":makeQuery(id+"F5.boolean.opBoolean","INTERSECT",EDGE,{"derivedFrom":[makeQuery(id+"F3.opLoft","SWEPT_FACE",FACE,{"disambiguationData":[OSD([sQuery(id+"F0.wireOp",EDGE,"E3"),sQuery(id+"F0.wireOp",EDGE,"E4.MirrorCS"),sQuery(id+"F0.wireOp",EDGE,"E9.filletArc"),sQuery(id+"F2.wireOp",EDGE,"E13.1.6"),sQuery(id+"F2.wireOp",EDGE,"E13.1.7"),sQuery(id+"F2.wireOp",EDGE,"E13.1.8")])]}),makeQuery(id+"F5.opExtrude","SWEPT_FACE",FACE,{"disambiguationData":[OSD([sQuery(id+"F4.wireOp",EDGE,"E14")])]})]}),"instanceName":"6"});
            var Q9;
            Q9=makeQuery(id+"F6.opPattern","COPY",EDGE,{"derivedFrom":makeQuery(id+"F5.boolean.opBoolean","INTERSECT",EDGE,{"derivedFrom":[makeQuery(id+"F3.opLoft","SWEPT_FACE",FACE,{"disambiguationData":[OSD([sQuery(id+"F0.wireOp",EDGE,"E0"),sQuery(id+"F0.wireOp",EDGE,"E6.MirrorCS"),sQuery(id+"F0.wireOp",EDGE,"E8.filletArc"),sQuery(id+"F2.wireOp",EDGE,"E11.0.0"),sQuery(id+"F2.wireOp",EDGE,"E13.1.3"),sQuery(id+"F2.wireOp",EDGE,"E13.1.4")])]}),makeQuery(id+"F5.opExtrude","SWEPT_FACE",FACE,{"disambiguationData":[OSD([sQuery(id+"F4.wireOp",EDGE,"E14")])]})]}),"instanceName":"6"});
            var Q10;
            Q10=makeQuery(id+"F6.opPattern","COPY",EDGE,{"derivedFrom":makeQuery(id+"F5.boolean.opBoolean","INTERSECT",EDGE,{"derivedFrom":[makeQuery(id+"F3.opLoft","SWEPT_FACE",FACE,{"disambiguationData":[OSD([sQuery(id+"F0.wireOp",EDGE,"E3"),sQuery(id+"F0.wireOp",EDGE,"E4.MirrorCS"),sQuery(id+"F0.wireOp",EDGE,"E9.filletArc"),sQuery(id+"F2.wireOp",EDGE,"E13.1.6"),sQuery(id+"F2.wireOp",EDGE,"E13.1.7"),sQuery(id+"F2.wireOp",EDGE,"E13.1.8")])]}),makeQuery(id+"F5.opExtrude","SWEPT_FACE",FACE,{"disambiguationData":[OSD([sQuery(id+"F4.wireOp",EDGE,"E14")])]})]}),"instanceName":"5"});
            var Q11;
            Q11=makeQuery(id+"F6.opPattern","COPY",EDGE,{"derivedFrom":makeQuery(id+"F5.boolean.opBoolean","INTERSECT",EDGE,{"derivedFrom":[makeQuery(id+"F3.opLoft","SWEPT_FACE",FACE,{"disambiguationData":[OSD([sQuery(id+"F0.wireOp",EDGE,"E0"),sQuery(id+"F0.wireOp",EDGE,"E6.MirrorCS"),sQuery(id+"F0.wireOp",EDGE,"E8.filletArc"),sQuery(id+"F2.wireOp",EDGE,"E11.0.0"),sQuery(id+"F2.wireOp",EDGE,"E13.1.3"),sQuery(id+"F2.wireOp",EDGE,"E13.1.4")])]}),makeQuery(id+"F5.opExtrude","SWEPT_FACE",FACE,{"disambiguationData":[OSD([sQuery(id+"F4.wireOp",EDGE,"E14")])]})]}),"instanceName":"5"});
            var Q12;
            Q12=makeQuery(id+"F6.opPattern","COPY",EDGE,{"derivedFrom":makeQuery(id+"F5.boolean.opBoolean","INTERSECT",EDGE,{"derivedFrom":[makeQuery(id+"F3.opLoft","SWEPT_FACE",FACE,{"disambiguationData":[OSD([sQuery(id+"F0.wireOp",EDGE,"E3"),sQuery(id+"F0.wireOp",EDGE,"E4.MirrorCS"),sQuery(id+"F0.wireOp",EDGE,"E9.filletArc"),sQuery(id+"F2.wireOp",EDGE,"E13.1.6"),sQuery(id+"F2.wireOp",EDGE,"E13.1.7"),sQuery(id+"F2.wireOp",EDGE,"E13.1.8")])]}),makeQuery(id+"F5.opExtrude","SWEPT_FACE",FACE,{"disambiguationData":[OSD([sQuery(id+"F4.wireOp",EDGE,"E14")])]})]}),"instanceName":"4"});
            var Q13;
            Q13=makeQuery(id+"F6.opPattern","COPY",EDGE,{"derivedFrom":makeQuery(id+"F5.boolean.opBoolean","INTERSECT",EDGE,{"derivedFrom":[makeQuery(id+"F3.opLoft","SWEPT_FACE",FACE,{"disambiguationData":[OSD([sQuery(id+"F0.wireOp",EDGE,"E0"),sQuery(id+"F0.wireOp",EDGE,"E6.MirrorCS"),sQuery(id+"F0.wireOp",EDGE,"E8.filletArc"),sQuery(id+"F2.wireOp",EDGE,"E11.0.0"),sQuery(id+"F2.wireOp",EDGE,"E13.1.3"),sQuery(id+"F2.wireOp",EDGE,"E13.1.4")])]}),makeQuery(id+"F5.opExtrude","SWEPT_FACE",FACE,{"disambiguationData":[OSD([sQuery(id+"F4.wireOp",EDGE,"E14")])]})]}),"instanceName":"4"});
            var Q14;
            Q14=makeQuery(id+"F6.opPattern","COPY",EDGE,{"derivedFrom":makeQuery(id+"F5.boolean.opBoolean","INTERSECT",EDGE,{"derivedFrom":[makeQuery(id+"F3.opLoft","SWEPT_FACE",FACE,{"disambiguationData":[OSD([sQuery(id+"F0.wireOp",EDGE,"E3"),sQuery(id+"F0.wireOp",EDGE,"E4.MirrorCS"),sQuery(id+"F0.wireOp",EDGE,"E9.filletArc"),sQuery(id+"F2.wireOp",EDGE,"E13.1.6"),sQuery(id+"F2.wireOp",EDGE,"E13.1.7"),sQuery(id+"F2.wireOp",EDGE,"E13.1.8")])]}),makeQuery(id+"F5.opExtrude","SWEPT_FACE",FACE,{"disambiguationData":[OSD([sQuery(id+"F4.wireOp",EDGE,"E14")])]})]}),"instanceName":"3"});
            var Q15;
            Q15=makeQuery(id+"F6.opPattern","COPY",EDGE,{"derivedFrom":makeQuery(id+"F5.boolean.opBoolean","INTERSECT",EDGE,{"derivedFrom":[makeQuery(id+"F3.opLoft","SWEPT_FACE",FACE,{"disambiguationData":[OSD([sQuery(id+"F0.wireOp",EDGE,"E0"),sQuery(id+"F0.wireOp",EDGE,"E6.MirrorCS"),sQuery(id+"F0.wireOp",EDGE,"E8.filletArc"),sQuery(id+"F2.wireOp",EDGE,"E11.0.0"),sQuery(id+"F2.wireOp",EDGE,"E13.1.3"),sQuery(id+"F2.wireOp",EDGE,"E13.1.4")])]}),makeQuery(id+"F5.opExtrude","SWEPT_FACE",FACE,{"disambiguationData":[OSD([sQuery(id+"F4.wireOp",EDGE,"E14")])]})]}),"instanceName":"3"});
            var Q16;
            Q16=makeQuery(id+"F6.opPattern","COPY",EDGE,{"derivedFrom":makeQuery(id+"F5.boolean.opBoolean","INTERSECT",EDGE,{"derivedFrom":[makeQuery(id+"F3.opLoft","SWEPT_FACE",FACE,{"disambiguationData":[OSD([sQuery(id+"F0.wireOp",EDGE,"E3"),sQuery(id+"F0.wireOp",EDGE,"E4.MirrorCS"),sQuery(id+"F0.wireOp",EDGE,"E9.filletArc"),sQuery(id+"F2.wireOp",EDGE,"E13.1.6"),sQuery(id+"F2.wireOp",EDGE,"E13.1.7"),sQuery(id+"F2.wireOp",EDGE,"E13.1.8")])]}),makeQuery(id+"F5.opExtrude","SWEPT_FACE",FACE,{"disambiguationData":[OSD([sQuery(id+"F4.wireOp",EDGE,"E14")])]})]}),"instanceName":"2"});
            var Q17;
            Q17=makeQuery(id+"F6.opPattern","COPY",EDGE,{"derivedFrom":makeQuery(id+"F5.boolean.opBoolean","INTERSECT",EDGE,{"derivedFrom":[makeQuery(id+"F3.opLoft","SWEPT_FACE",FACE,{"disambiguationData":[OSD([sQuery(id+"F0.wireOp",EDGE,"E0"),sQuery(id+"F0.wireOp",EDGE,"E6.MirrorCS"),sQuery(id+"F0.wireOp",EDGE,"E8.filletArc"),sQuery(id+"F2.wireOp",EDGE,"E11.0.0"),sQuery(id+"F2.wireOp",EDGE,"E13.1.3"),sQuery(id+"F2.wireOp",EDGE,"E13.1.4")])]}),makeQuery(id+"F5.opExtrude","SWEPT_FACE",FACE,{"disambiguationData":[OSD([sQuery(id+"F4.wireOp",EDGE,"E14")])]})]}),"instanceName":"2"});
            var Q18;
            Q18=makeQuery(id+"F6.opPattern","COPY",EDGE,{"derivedFrom":makeQuery(id+"F5.boolean.opBoolean","INTERSECT",EDGE,{"derivedFrom":[makeQuery(id+"F3.opLoft","SWEPT_FACE",FACE,{"disambiguationData":[OSD([sQuery(id+"F0.wireOp",EDGE,"E0"),sQuery(id+"F0.wireOp",EDGE,"E6.MirrorCS"),sQuery(id+"F0.wireOp",EDGE,"E8.filletArc"),sQuery(id+"F2.wireOp",EDGE,"E11.0.0"),sQuery(id+"F2.wireOp",EDGE,"E13.1.3"),sQuery(id+"F2.wireOp",EDGE,"E13.1.4")])]}),makeQuery(id+"F5.opExtrude","SWEPT_FACE",FACE,{"disambiguationData":[OSD([sQuery(id+"F4.wireOp",EDGE,"E14")])]})]}),"instanceName":"1"});
            var Q19;
            Q19=makeQuery(id+"F6.opPattern","COPY",EDGE,{"derivedFrom":makeQuery(id+"F5.boolean.opBoolean","INTERSECT",EDGE,{"derivedFrom":[makeQuery(id+"F3.opLoft","SWEPT_FACE",FACE,{"disambiguationData":[OSD([sQuery(id+"F0.wireOp",EDGE,"E3"),sQuery(id+"F0.wireOp",EDGE,"E4.MirrorCS"),sQuery(id+"F0.wireOp",EDGE,"E9.filletArc"),sQuery(id+"F2.wireOp",EDGE,"E13.1.6"),sQuery(id+"F2.wireOp",EDGE,"E13.1.7"),sQuery(id+"F2.wireOp",EDGE,"E13.1.8")])]}),makeQuery(id+"F5.opExtrude","SWEPT_FACE",FACE,{"disambiguationData":[OSD([sQuery(id+"F4.wireOp",EDGE,"E14")])]})]}),"instanceName":"10"});
            var Q20;
            Q20=makeQuery(id+"F6.opPattern","COPY",EDGE,{"derivedFrom":makeQuery(id+"F5.boolean.opBoolean","INTERSECT",EDGE,{"derivedFrom":[makeQuery(id+"F3.opLoft","SWEPT_FACE",FACE,{"disambiguationData":[OSD([sQuery(id+"F0.wireOp",EDGE,"E3"),sQuery(id+"F0.wireOp",EDGE,"E4.MirrorCS"),sQuery(id+"F0.wireOp",EDGE,"E9.filletArc"),sQuery(id+"F2.wireOp",EDGE,"E13.1.6"),sQuery(id+"F2.wireOp",EDGE,"E13.1.7"),sQuery(id+"F2.wireOp",EDGE,"E13.1.8")])]}),makeQuery(id+"F5.opExtrude","SWEPT_FACE",FACE,{"disambiguationData":[OSD([sQuery(id+"F4.wireOp",EDGE,"E14")])]})]}),"instanceName":"11"});
            var Q21;
            Q21=makeQuery(id+"F6.opPattern","COPY",EDGE,{"derivedFrom":makeQuery(id+"F5.boolean.opBoolean","INTERSECT",EDGE,{"derivedFrom":[makeQuery(id+"F3.opLoft","SWEPT_FACE",FACE,{"disambiguationData":[OSD([sQuery(id+"F0.wireOp",EDGE,"E3"),sQuery(id+"F0.wireOp",EDGE,"E4.MirrorCS"),sQuery(id+"F0.wireOp",EDGE,"E9.filletArc"),sQuery(id+"F2.wireOp",EDGE,"E13.1.6"),sQuery(id+"F2.wireOp",EDGE,"E13.1.7"),sQuery(id+"F2.wireOp",EDGE,"E13.1.8")])]}),makeQuery(id+"F5.opExtrude","SWEPT_FACE",FACE,{"disambiguationData":[OSD([sQuery(id+"F4.wireOp",EDGE,"E14")])]})]}),"instanceName":"12"});
            var Q22;
            Q22=makeQuery(id+"F6.opPattern","COPY",EDGE,{"derivedFrom":makeQuery(id+"F5.boolean.opBoolean","INTERSECT",EDGE,{"derivedFrom":[makeQuery(id+"F3.opLoft","SWEPT_FACE",FACE,{"disambiguationData":[OSD([sQuery(id+"F0.wireOp",EDGE,"E3"),sQuery(id+"F0.wireOp",EDGE,"E4.MirrorCS"),sQuery(id+"F0.wireOp",EDGE,"E9.filletArc"),sQuery(id+"F2.wireOp",EDGE,"E13.1.6"),sQuery(id+"F2.wireOp",EDGE,"E13.1.7"),sQuery(id+"F2.wireOp",EDGE,"E13.1.8")])]}),makeQuery(id+"F5.opExtrude","SWEPT_FACE",FACE,{"disambiguationData":[OSD([sQuery(id+"F4.wireOp",EDGE,"E14")])]})]}),"instanceName":"13"});
            var Q23;
            Q23=makeQuery(id+"F6.opPattern","COPY",EDGE,{"derivedFrom":makeQuery(id+"F5.boolean.opBoolean","INTERSECT",EDGE,{"derivedFrom":[makeQuery(id+"F3.opLoft","SWEPT_FACE",FACE,{"disambiguationData":[OSD([sQuery(id+"F0.wireOp",EDGE,"E3"),sQuery(id+"F0.wireOp",EDGE,"E4.MirrorCS"),sQuery(id+"F0.wireOp",EDGE,"E9.filletArc"),sQuery(id+"F2.wireOp",EDGE,"E13.1.6"),sQuery(id+"F2.wireOp",EDGE,"E13.1.7"),sQuery(id+"F2.wireOp",EDGE,"E13.1.8")])]}),makeQuery(id+"F5.opExtrude","SWEPT_FACE",FACE,{"disambiguationData":[OSD([sQuery(id+"F4.wireOp",EDGE,"E14")])]})]}),"instanceName":"14"});
            var Q24;
            Q24=makeQuery(id+"F5.boolean.opBoolean","INTERSECT",EDGE,{"derivedFrom":[makeQuery(id+"F3.opLoft","SWEPT_FACE",FACE,{"disambiguationData":[OSD([sQuery(id+"F0.wireOp",EDGE,"E3"),sQuery(id+"F0.wireOp",EDGE,"E4.MirrorCS"),sQuery(id+"F0.wireOp",EDGE,"E9.filletArc"),sQuery(id+"F2.wireOp",EDGE,"E13.1.6"),sQuery(id+"F2.wireOp",EDGE,"E13.1.7"),sQuery(id+"F2.wireOp",EDGE,"E13.1.8")])]}),makeQuery(id+"F5.opExtrude","SWEPT_FACE",FACE,{"disambiguationData":[OSD([sQuery(id+"F4.wireOp",EDGE,"E14")])]})]});
            var Q25;
            Q25=makeQuery(id+"F5.boolean.opBoolean","INTERSECT",EDGE,{"derivedFrom":[makeQuery(id+"F3.opLoft","SWEPT_FACE",FACE,{"disambiguationData":[OSD([sQuery(id+"F0.wireOp",EDGE,"E0"),sQuery(id+"F0.wireOp",EDGE,"E6.MirrorCS"),sQuery(id+"F0.wireOp",EDGE,"E8.filletArc"),sQuery(id+"F2.wireOp",EDGE,"E11.0.0"),sQuery(id+"F2.wireOp",EDGE,"E13.1.3"),sQuery(id+"F2.wireOp",EDGE,"E13.1.4")])]}),makeQuery(id+"F5.opExtrude","SWEPT_FACE",FACE,{"disambiguationData":[OSD([sQuery(id+"F4.wireOp",EDGE,"E14")])]})]});
            var Q26;
            Q26=makeQuery(id+"F6.opPattern","COPY",EDGE,{"derivedFrom":makeQuery(id+"F5.boolean.opBoolean","INTERSECT",EDGE,{"derivedFrom":[makeQuery(id+"F3.opLoft","SWEPT_FACE",FACE,{"disambiguationData":[OSD([sQuery(id+"F0.wireOp",EDGE,"E0"),sQuery(id+"F0.wireOp",EDGE,"E6.MirrorCS"),sQuery(id+"F0.wireOp",EDGE,"E8.filletArc"),sQuery(id+"F2.wireOp",EDGE,"E11.0.0"),sQuery(id+"F2.wireOp",EDGE,"E13.1.3"),sQuery(id+"F2.wireOp",EDGE,"E13.1.4")])]}),makeQuery(id+"F5.opExtrude","SWEPT_FACE",FACE,{"disambiguationData":[OSD([sQuery(id+"F4.wireOp",EDGE,"E14")])]})]}),"instanceName":"13"});
            var Q27;
            Q27=makeQuery(id+"F6.opPattern","COPY",EDGE,{"derivedFrom":makeQuery(id+"F5.boolean.opBoolean","INTERSECT",EDGE,{"derivedFrom":[makeQuery(id+"F3.opLoft","SWEPT_FACE",FACE,{"disambiguationData":[OSD([sQuery(id+"F0.wireOp",EDGE,"E0"),sQuery(id+"F0.wireOp",EDGE,"E6.MirrorCS"),sQuery(id+"F0.wireOp",EDGE,"E8.filletArc"),sQuery(id+"F2.wireOp",EDGE,"E11.0.0"),sQuery(id+"F2.wireOp",EDGE,"E13.1.3"),sQuery(id+"F2.wireOp",EDGE,"E13.1.4")])]}),makeQuery(id+"F5.opExtrude","SWEPT_FACE",FACE,{"disambiguationData":[OSD([sQuery(id+"F4.wireOp",EDGE,"E14")])]})]}),"instanceName":"12"});
            var Q28;
            Q28=makeQuery(id+"F6.opPattern","COPY",EDGE,{"derivedFrom":makeQuery(id+"F5.boolean.opBoolean","INTERSECT",EDGE,{"derivedFrom":[makeQuery(id+"F3.opLoft","SWEPT_FACE",FACE,{"disambiguationData":[OSD([sQuery(id+"F0.wireOp",EDGE,"E0"),sQuery(id+"F0.wireOp",EDGE,"E6.MirrorCS"),sQuery(id+"F0.wireOp",EDGE,"E8.filletArc"),sQuery(id+"F2.wireOp",EDGE,"E11.0.0"),sQuery(id+"F2.wireOp",EDGE,"E13.1.3"),sQuery(id+"F2.wireOp",EDGE,"E13.1.4")])]}),makeQuery(id+"F5.opExtrude","SWEPT_FACE",FACE,{"disambiguationData":[OSD([sQuery(id+"F4.wireOp",EDGE,"E14")])]})]}),"instanceName":"11"});
            var Q29;
            Q29=makeQuery(id+"F6.opPattern","COPY",EDGE,{"derivedFrom":makeQuery(id+"F5.boolean.opBoolean","INTERSECT",EDGE,{"derivedFrom":[makeQuery(id+"F3.opLoft","SWEPT_FACE",FACE,{"disambiguationData":[OSD([sQuery(id+"F0.wireOp",EDGE,"E0"),sQuery(id+"F0.wireOp",EDGE,"E6.MirrorCS"),sQuery(id+"F0.wireOp",EDGE,"E8.filletArc"),sQuery(id+"F2.wireOp",EDGE,"E11.0.0"),sQuery(id+"F2.wireOp",EDGE,"E13.1.3"),sQuery(id+"F2.wireOp",EDGE,"E13.1.4")])]}),makeQuery(id+"F5.opExtrude","SWEPT_FACE",FACE,{"disambiguationData":[OSD([sQuery(id+"F4.wireOp",EDGE,"E14")])]})]}),"instanceName":"14"});
            fillet(context, id + "F7", {"entities" : qUnion([Q0, Q1, Q2, Q3, Q4, Q5, Q6, Q7, Q8, Q9, Q10, Q11, Q12, Q13, Q14, Q15, Q16, Q17, Q18, Q19, Q20, Q21, Q22, Q23, Q24, Q25, Q26, Q27, Q28, Q29]), "radius" : 1.6 * mm, "tangentPropagation" : true, "allowEdgeOverflow" : false});
        }
        {
            var Q0;
            {var subQ0=sQuery(id+"F2.wireOp",EDGE,"E13.1.0");Q0=makeQuery(id+"F6.opPattern","COPY",BODY,{"derivedFrom":makeQuery(id+"F3.opLoft","SWEPT_BODY",BODY,{"disambiguationData":[OSD([makeQuery(id+"F0.imprint","IMPRINT",FACE,{"disambiguationData":[TD([[makeQuery(id+"F0.imprint","IMPRINT",EDGE,{"derivedFrom":sQuery(id+"F0.wireOp",EDGE,"E1.trimOffspring")}),1.0]])]}),makeQuery(id+"F2.imprint","IMPRINT",FACE,{"disambiguationData":[TD([[makeQuery(id+"F2.imprint","IMPRINT",EDGE,{"derivedFrom":subQ0}),1.0]])]})])]}),"instanceName":"14"});}
            var Q1;
            {var subQ0=sQuery(id+"F2.wireOp",EDGE,"E13.1.0");Q1=makeQuery(id+"F3.opLoft","SWEPT_BODY",BODY,{"disambiguationData":[OSD([makeQuery(id+"F0.imprint","IMPRINT",FACE,{"disambiguationData":[TD([[makeQuery(id+"F0.imprint","IMPRINT",EDGE,{"derivedFrom":sQuery(id+"F0.wireOp",EDGE,"E1.trimOffspring")}),1.0]])]}),makeQuery(id+"F2.imprint","IMPRINT",FACE,{"disambiguationData":[TD([[makeQuery(id+"F2.imprint","IMPRINT",EDGE,{"derivedFrom":subQ0}),1.0]])]})])]});}
            var Q2;
            {var subQ0=sQuery(id+"F2.wireOp",EDGE,"E13.1.0");Q2=makeQuery(id+"F6.opPattern","COPY",BODY,{"derivedFrom":makeQuery(id+"F3.opLoft","SWEPT_BODY",BODY,{"disambiguationData":[OSD([makeQuery(id+"F0.imprint","IMPRINT",FACE,{"disambiguationData":[TD([[makeQuery(id+"F0.imprint","IMPRINT",EDGE,{"derivedFrom":sQuery(id+"F0.wireOp",EDGE,"E1.trimOffspring")}),1.0]])]}),makeQuery(id+"F2.imprint","IMPRINT",FACE,{"disambiguationData":[TD([[makeQuery(id+"F2.imprint","IMPRINT",EDGE,{"derivedFrom":subQ0}),1.0]])]})])]}),"instanceName":"1"});}
            var Q3;
            {var subQ0=sQuery(id+"F2.wireOp",EDGE,"E13.1.0");Q3=makeQuery(id+"F6.opPattern","COPY",BODY,{"derivedFrom":makeQuery(id+"F3.opLoft","SWEPT_BODY",BODY,{"disambiguationData":[OSD([makeQuery(id+"F0.imprint","IMPRINT",FACE,{"disambiguationData":[TD([[makeQuery(id+"F0.imprint","IMPRINT",EDGE,{"derivedFrom":sQuery(id+"F0.wireOp",EDGE,"E1.trimOffspring")}),1.0]])]}),makeQuery(id+"F2.imprint","IMPRINT",FACE,{"disambiguationData":[TD([[makeQuery(id+"F2.imprint","IMPRINT",EDGE,{"derivedFrom":subQ0}),1.0]])]})])]}),"instanceName":"2"});}
            var Q4;
            {var subQ0=sQuery(id+"F2.wireOp",EDGE,"E13.1.0");Q4=makeQuery(id+"F6.opPattern","COPY",BODY,{"derivedFrom":makeQuery(id+"F3.opLoft","SWEPT_BODY",BODY,{"disambiguationData":[OSD([makeQuery(id+"F0.imprint","IMPRINT",FACE,{"disambiguationData":[TD([[makeQuery(id+"F0.imprint","IMPRINT",EDGE,{"derivedFrom":sQuery(id+"F0.wireOp",EDGE,"E1.trimOffspring")}),1.0]])]}),makeQuery(id+"F2.imprint","IMPRINT",FACE,{"disambiguationData":[TD([[makeQuery(id+"F2.imprint","IMPRINT",EDGE,{"derivedFrom":subQ0}),1.0]])]})])]}),"instanceName":"3"});}
            var Q5;
            {var subQ0=sQuery(id+"F2.wireOp",EDGE,"E13.1.0");Q5=makeQuery(id+"F6.opPattern","COPY",BODY,{"derivedFrom":makeQuery(id+"F3.opLoft","SWEPT_BODY",BODY,{"disambiguationData":[OSD([makeQuery(id+"F0.imprint","IMPRINT",FACE,{"disambiguationData":[TD([[makeQuery(id+"F0.imprint","IMPRINT",EDGE,{"derivedFrom":sQuery(id+"F0.wireOp",EDGE,"E1.trimOffspring")}),1.0]])]}),makeQuery(id+"F2.imprint","IMPRINT",FACE,{"disambiguationData":[TD([[makeQuery(id+"F2.imprint","IMPRINT",EDGE,{"derivedFrom":subQ0}),1.0]])]})])]}),"instanceName":"4"});}
            var Q6;
            {var subQ0=sQuery(id+"F2.wireOp",EDGE,"E13.1.0");Q6=makeQuery(id+"F6.opPattern","COPY",BODY,{"derivedFrom":makeQuery(id+"F3.opLoft","SWEPT_BODY",BODY,{"disambiguationData":[OSD([makeQuery(id+"F0.imprint","IMPRINT",FACE,{"disambiguationData":[TD([[makeQuery(id+"F0.imprint","IMPRINT",EDGE,{"derivedFrom":sQuery(id+"F0.wireOp",EDGE,"E1.trimOffspring")}),1.0]])]}),makeQuery(id+"F2.imprint","IMPRINT",FACE,{"disambiguationData":[TD([[makeQuery(id+"F2.imprint","IMPRINT",EDGE,{"derivedFrom":subQ0}),1.0]])]})])]}),"instanceName":"5"});}
            var Q7;
            {var subQ0=sQuery(id+"F2.wireOp",EDGE,"E13.1.0");Q7=makeQuery(id+"F6.opPattern","COPY",BODY,{"derivedFrom":makeQuery(id+"F3.opLoft","SWEPT_BODY",BODY,{"disambiguationData":[OSD([makeQuery(id+"F0.imprint","IMPRINT",FACE,{"disambiguationData":[TD([[makeQuery(id+"F0.imprint","IMPRINT",EDGE,{"derivedFrom":sQuery(id+"F0.wireOp",EDGE,"E1.trimOffspring")}),1.0]])]}),makeQuery(id+"F2.imprint","IMPRINT",FACE,{"disambiguationData":[TD([[makeQuery(id+"F2.imprint","IMPRINT",EDGE,{"derivedFrom":subQ0}),1.0]])]})])]}),"instanceName":"6"});}
            var Q8;
            {var subQ0=sQuery(id+"F2.wireOp",EDGE,"E13.1.0");Q8=makeQuery(id+"F6.opPattern","COPY",BODY,{"derivedFrom":makeQuery(id+"F3.opLoft","SWEPT_BODY",BODY,{"disambiguationData":[OSD([makeQuery(id+"F0.imprint","IMPRINT",FACE,{"disambiguationData":[TD([[makeQuery(id+"F0.imprint","IMPRINT",EDGE,{"derivedFrom":sQuery(id+"F0.wireOp",EDGE,"E1.trimOffspring")}),1.0]])]}),makeQuery(id+"F2.imprint","IMPRINT",FACE,{"disambiguationData":[TD([[makeQuery(id+"F2.imprint","IMPRINT",EDGE,{"derivedFrom":subQ0}),1.0]])]})])]}),"instanceName":"7"});}
            var Q9;
            {var subQ0=sQuery(id+"F2.wireOp",EDGE,"E13.1.0");Q9=makeQuery(id+"F6.opPattern","COPY",BODY,{"derivedFrom":makeQuery(id+"F3.opLoft","SWEPT_BODY",BODY,{"disambiguationData":[OSD([makeQuery(id+"F0.imprint","IMPRINT",FACE,{"disambiguationData":[TD([[makeQuery(id+"F0.imprint","IMPRINT",EDGE,{"derivedFrom":sQuery(id+"F0.wireOp",EDGE,"E1.trimOffspring")}),1.0]])]}),makeQuery(id+"F2.imprint","IMPRINT",FACE,{"disambiguationData":[TD([[makeQuery(id+"F2.imprint","IMPRINT",EDGE,{"derivedFrom":subQ0}),1.0]])]})])]}),"instanceName":"9"});}
            var Q10;
            {var subQ0=sQuery(id+"F2.wireOp",EDGE,"E13.1.0");Q10=makeQuery(id+"F6.opPattern","COPY",BODY,{"derivedFrom":makeQuery(id+"F3.opLoft","SWEPT_BODY",BODY,{"disambiguationData":[OSD([makeQuery(id+"F0.imprint","IMPRINT",FACE,{"disambiguationData":[TD([[makeQuery(id+"F0.imprint","IMPRINT",EDGE,{"derivedFrom":sQuery(id+"F0.wireOp",EDGE,"E1.trimOffspring")}),1.0]])]}),makeQuery(id+"F2.imprint","IMPRINT",FACE,{"disambiguationData":[TD([[makeQuery(id+"F2.imprint","IMPRINT",EDGE,{"derivedFrom":subQ0}),1.0]])]})])]}),"instanceName":"10"});}
            var Q11;
            {var subQ0=sQuery(id+"F2.wireOp",EDGE,"E13.1.0");Q11=makeQuery(id+"F6.opPattern","COPY",BODY,{"derivedFrom":makeQuery(id+"F3.opLoft","SWEPT_BODY",BODY,{"disambiguationData":[OSD([makeQuery(id+"F0.imprint","IMPRINT",FACE,{"disambiguationData":[TD([[makeQuery(id+"F0.imprint","IMPRINT",EDGE,{"derivedFrom":sQuery(id+"F0.wireOp",EDGE,"E1.trimOffspring")}),1.0]])]}),makeQuery(id+"F2.imprint","IMPRINT",FACE,{"disambiguationData":[TD([[makeQuery(id+"F2.imprint","IMPRINT",EDGE,{"derivedFrom":subQ0}),1.0]])]})])]}),"instanceName":"11"});}
            var Q12;
            {var subQ0=sQuery(id+"F2.wireOp",EDGE,"E13.1.0");Q12=makeQuery(id+"F6.opPattern","COPY",BODY,{"derivedFrom":makeQuery(id+"F3.opLoft","SWEPT_BODY",BODY,{"disambiguationData":[OSD([makeQuery(id+"F0.imprint","IMPRINT",FACE,{"disambiguationData":[TD([[makeQuery(id+"F0.imprint","IMPRINT",EDGE,{"derivedFrom":sQuery(id+"F0.wireOp",EDGE,"E1.trimOffspring")}),1.0]])]}),makeQuery(id+"F2.imprint","IMPRINT",FACE,{"disambiguationData":[TD([[makeQuery(id+"F2.imprint","IMPRINT",EDGE,{"derivedFrom":subQ0}),1.0]])]})])]}),"instanceName":"12"});}
            var Q13;
            {var subQ0=sQuery(id+"F2.wireOp",EDGE,"E13.1.0");Q13=makeQuery(id+"F6.opPattern","COPY",BODY,{"derivedFrom":makeQuery(id+"F3.opLoft","SWEPT_BODY",BODY,{"disambiguationData":[OSD([makeQuery(id+"F0.imprint","IMPRINT",FACE,{"disambiguationData":[TD([[makeQuery(id+"F0.imprint","IMPRINT",EDGE,{"derivedFrom":sQuery(id+"F0.wireOp",EDGE,"E1.trimOffspring")}),1.0]])]}),makeQuery(id+"F2.imprint","IMPRINT",FACE,{"disambiguationData":[TD([[makeQuery(id+"F2.imprint","IMPRINT",EDGE,{"derivedFrom":subQ0}),1.0]])]})])]}),"instanceName":"13"});}
            var Q14;
            {var subQ0=sQuery(id+"F2.wireOp",EDGE,"E13.1.0");Q14=makeQuery(id+"F6.opPattern","COPY",BODY,{"derivedFrom":makeQuery(id+"F3.opLoft","SWEPT_BODY",BODY,{"disambiguationData":[OSD([makeQuery(id+"F0.imprint","IMPRINT",FACE,{"disambiguationData":[TD([[makeQuery(id+"F0.imprint","IMPRINT",EDGE,{"derivedFrom":sQuery(id+"F0.wireOp",EDGE,"E1.trimOffspring")}),1.0]])]}),makeQuery(id+"F2.imprint","IMPRINT",FACE,{"disambiguationData":[TD([[makeQuery(id+"F2.imprint","IMPRINT",EDGE,{"derivedFrom":subQ0}),1.0]])]})])]}),"instanceName":"8"});}
            booleanBodies(context, id + "F8", {"operationType" : BooleanOperationType.UNION, "tools" : qUnion([Q0, Q1, Q2, Q3, Q4, Q5, Q6, Q7, Q8, Q9, Q10, Q11, Q12, Q13, Q14])});
        }
        {
            var Q0;
            {var subQ0=sQuery(id+"F2.wireOp",EDGE,"E13.1.0");var subQ3=makeQuery(id+"F2.imprint","IMPRINT",FACE,{"disambiguationData":[TD([[makeQuery(id+"F2.imprint","IMPRINT",EDGE,{"derivedFrom":subQ0}),1.0]])]});var subQ4=makeQuery(id+"F5.boolean.opBoolean","MERGE",FACE,{"derivedFrom":[makeQuery(id+"F3.opLoft","CAP_FACE",FACE,{"disambiguationData":[OSD([subQ3])],"isStart":true}),makeQuery(id+"F5.opExtrude","CAP_FACE",FACE,{"disambiguationData":[OSD([subQ3])],"isStart":false})]});Q0=makeQuery(id+"F8.opBoolean","MERGE",FACE,{"derivedFrom":[subQ4,makeQuery(id+"F6.opPattern","COPY",FACE,{"derivedFrom":subQ4,"instanceName":"1"}),makeQuery(id+"F6.opPattern","COPY",FACE,{"derivedFrom":subQ4,"instanceName":"2"}),makeQuery(id+"F6.opPattern","COPY",FACE,{"derivedFrom":subQ4,"instanceName":"3"}),makeQuery(id+"F6.opPattern","COPY",FACE,{"derivedFrom":subQ4,"instanceName":"4"}),makeQuery(id+"F6.opPattern","COPY",FACE,{"derivedFrom":subQ4,"instanceName":"5"}),makeQuery(id+"F6.opPattern","COPY",FACE,{"derivedFrom":subQ4,"instanceName":"6"}),makeQuery(id+"F6.opPattern","COPY",FACE,{"derivedFrom":subQ4,"instanceName":"7"}),makeQuery(id+"F6.opPattern","COPY",FACE,{"derivedFrom":subQ4,"instanceName":"8"}),makeQuery(id+"F6.opPattern","COPY",FACE,{"derivedFrom":subQ4,"instanceName":"9"}),makeQuery(id+"F6.opPattern","COPY",FACE,{"derivedFrom":subQ4,"instanceName":"10"}),makeQuery(id+"F6.opPattern","COPY",FACE,{"derivedFrom":subQ4,"instanceName":"11"}),makeQuery(id+"F6.opPattern","COPY",FACE,{"derivedFrom":subQ4,"instanceName":"12"}),makeQuery(id+"F6.opPattern","COPY",FACE,{"derivedFrom":subQ4,"instanceName":"13"}),makeQuery(id+"F6.opPattern","COPY",FACE,{"derivedFrom":subQ4,"instanceName":"14"})]});}
            var sketch = newSketch(context, id + "F9", { "sketchPlane" : qUnion([Q0])});
            skCircle(sketch, "E15", {"center": v(0, 0) * mm, "radius": 6.35 * mm});
            skSolve(sketch);
        }
        {
            var Q0;
            Q0 = qSketchRegion(id + "F9", true);
            extrude(context, id + "F10", {"entities" : qUnion([Q0]), "operationType" : NewBodyOperationType.REMOVE, "endBound" : BoundingType.THROUGH_ALL, "oppositeDirection" : true, "depth" : 25.4 * mm});
        }
    });
